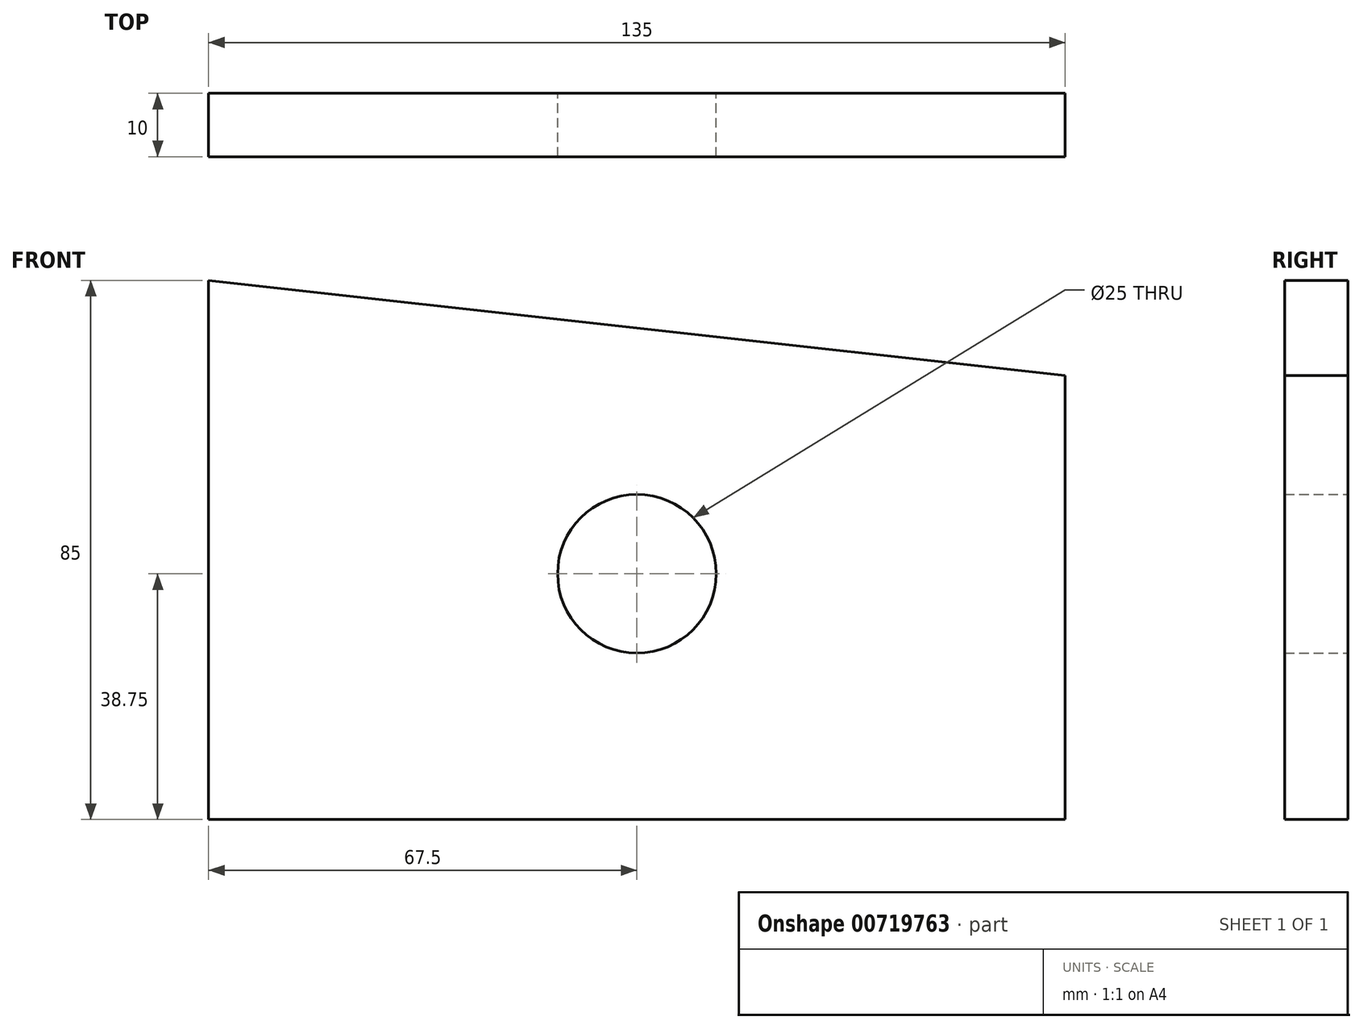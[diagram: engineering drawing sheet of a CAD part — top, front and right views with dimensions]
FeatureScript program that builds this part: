
annotation { "Feature Type Name" : "Feature", "Feature Type Description" : "" }
export const myFeature = defineFeature(function(context is Context, id is Id, definition is map)
    precondition{}
    {
        {
            var Q0;
            Q0=qCreatedBy(makeId("Front.planeOp"),FACE);
            var sketch = newSketch(context, id + "F0", { "sketchPlane" : qUnion([Q0])});
            skLineSegment(sketch, "E0", {"start": v(0, 0) * mm, "end": v(0, 70) * mm});
            skLineSegment(sketch, "E1", {"start": v(0, 70) * mm, "end": v(-135, 85) * mm});
            skLineSegment(sketch, "E2", {"start": v(0, 0) * mm, "end": v(-135, 0) * mm});
            skLineSegment(sketch, "E3", {"start": v(-135, 0) * mm, "end": v(-135, 85) * mm});
            skCircle(sketch, "E4", {"center": v(-67.5, 38.75) * mm, "radius": 12.5 * mm});
            skLineSegment(sketch, "E5", {"start": v(-67.5, 38.75) * mm, "end": v(-67.5, 77.5) * mm});
            skSolve(sketch);
        }
        {
            var Q0;
            Q0 = qSketchRegion(id + "F0", true);
            extrude(context, id + "F1", {"entities" : qUnion([Q0]), "depth" : 10 * mm, "offsetDistance" : 25 * mm});
        }
    });
